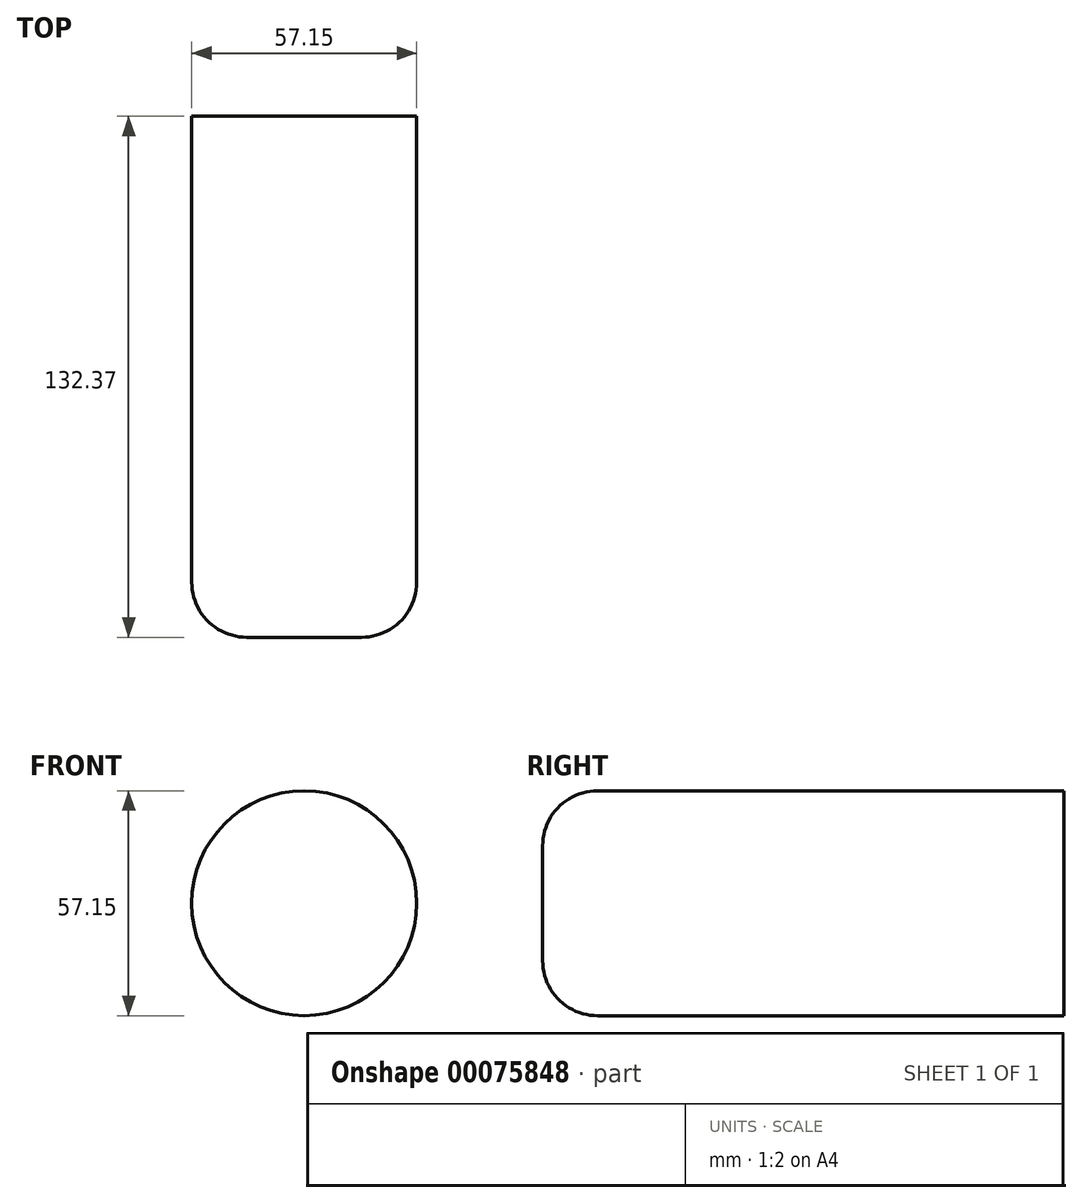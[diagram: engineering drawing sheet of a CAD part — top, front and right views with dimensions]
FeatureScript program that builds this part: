
annotation { "Feature Type Name" : "Feature", "Feature Type Description" : "" }
export const myFeature = defineFeature(function(context is Context, id is Id, definition is map)
    precondition{}
    {
        {
            var Q0;
            Q0=qCreatedBy(makeId("Front.planeOp"),FACE);
            var sketch = newSketch(context, id + "F0", { "sketchPlane" : qUnion([Q0])});
            skCircle(sketch, "E0", {"center": v(-50.8, 25.4) * mm, "radius": 28.57 * mm});
            skSolve(sketch);
        }
        {
            var Q0;
            Q0=makeQuery(id+"F0.imprint","IMPRINT",FACE,{"disambiguationData":[TD([[makeQuery(id+"F0.imprint","IMPRINT",EDGE,{"derivedFrom":sQuery(id+"F0.wireOp",EDGE,"E0")}),1.0]])]});
            extrude(context, id + "F1", {"entities" : qUnion([Q0]), "depth" : 132.37 * mm});
        }
        {
            var Q0;
            Q0=makeQuery(id+"F1.opExtrude","CAP_FACE",FACE,{"disambiguationData":[OSD([sQuery(id+"F0.wireOp",EDGE,"E0")])],"isStart":false});
            var sketch = newSketch(context, id + "F2", { "sketchPlane" : qUnion([Q0])});
            skCircle(sketch, "E1", {"center": v(-50.8, 25.4) * mm, "radius": 20.95 * mm});
            skSolve(sketch);
        }
        {
            var Q0;
            Q0 = qSketchRegion(id + "F2", true);
            extrude(context, id + "F3", {"entities" : qUnion([Q0]), "operationType" : NewBodyOperationType.ADD, "oppositeDirection" : true, "depth" : 17.42 * mm});
        }
        {
            var Q0;
            Q0=makeQuery(id+"F1.opExtrude","CAP_FACE",FACE,{"disambiguationData":[OSD([sQuery(id+"F0.wireOp",EDGE,"E0")])],"isStart":false});
            var Q1;
            Q1=makeQuery(id+"F1.opExtrude","CAP_EDGE",EDGE,{"disambiguationData":[OSD([sQuery(id+"F0.wireOp",EDGE,"E0")])],"isStart":false});
            fillet(context, id + "F4", {"entities" : qUnion([Q0, Q1]), "radius" : 13.96 * mm, "tangentPropagation" : true, "allowEdgeOverflow" : false});
        }
    });
